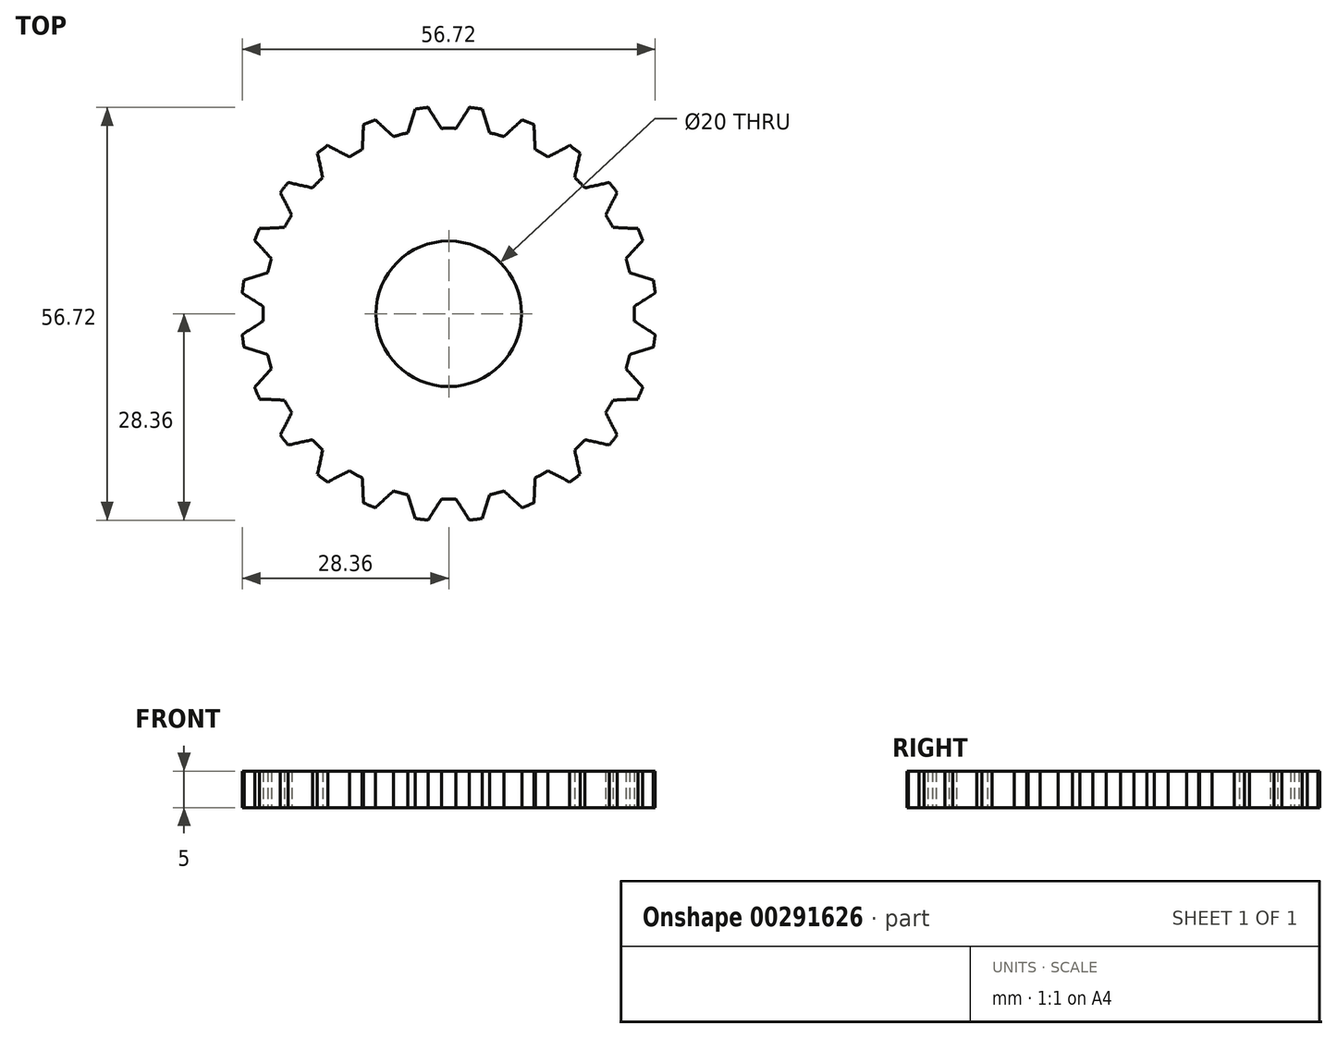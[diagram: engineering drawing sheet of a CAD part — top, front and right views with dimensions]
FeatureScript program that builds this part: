
annotation { "Feature Type Name" : "Feature", "Feature Type Description" : "" }
export const myFeature = defineFeature(function(context is Context, id is Id, definition is map)
    precondition{}
    {
        {
            assignVariable(context, id + "F0", {"name" : "pin", "anyValue" : 24});
        }
        {
            assignVariable(context, id + "F1", {"name" : "Thickness", "anyValue" : 5});
        }
        {
            var Q0;
            Q0=qCreatedBy(makeId("Front.planeOp"),FACE);
            var sketch = newSketch(context, id + "F2", { "sketchPlane" : qUnion([Q0])});
            skLineSegment(sketch, "E0", {"start": v(0, 0) * mm, "end": v(0, 5) * mm, "construction": true});
            skSolve(sketch);
        }
        {
            var Q0;
            Q0=qCreatedBy(makeId("Top.planeOp"),FACE);
            var sketch = newSketch(context, id + "F3", { "sketchPlane" : qUnion([Q0])});
            skCircle(sketch, "E1", {"center": v(0, 0) * mm, "radius": 24 * mm, "construction": true});
            skLineSegment(sketch, "E2", {"start": v(0, 0) * mm, "end": v(24, 0) * mm, "construction": true});
            skLineSegment(sketch, "E3", {"start": v(0, 0) * mm, "end": v(23.18, 6.21) * mm, "construction": true});
            skLineSegment(sketch, "E4", {"start": v(23.18, 6.21) * mm, "end": v(24, 0) * mm, "construction": true});
            skLineSegment(sketch, "E5", {"start": v(0, 0) * mm, "end": v(23.6, 3.1) * mm, "construction": true});
            skLineSegment(sketch, "E6", {"start": v(23.18, 6.21) * mm, "end": v(29.74, 3.92) * mm, "construction": true});
            skLineSegment(sketch, "E7", {"start": v(29.74, 3.92) * mm, "end": v(24, 0) * mm, "construction": true});
            skFitSpline(sketch, "E8", {"points": [v(23.18, 6.21) * mm, v(29.74, 3.92) * mm, v(24, 0) * mm], "startDerivative": vector(29.8, -10.5) * mm, "endDerivative": vector(-26.07, -17.85) * mm});
            skCircle(sketch, "E9", {"center": v(0, 0) * mm, "radius": 10 * mm});
            skLineSegment(sketch, "E10", {"start": v(29.74, 3.92) * mm, "end": v(23.8, 3.13) * mm, "construction": true});
            skCircle(sketch, "E11", {"center": v(0, 0) * mm, "radius": 28.5 * mm});
            skCircle(sketch, "E12", {"center": v(0, 0) * mm, "radius": 25.5 * mm});
            skLineSegment(sketch, "E13", {"start": v(28.15, 4.46) * mm, "end": v(28.34, 2.98) * mm, "construction": true});
            skSolve(sketch);
        }
        {
            var Q0;
            Q0=makeQuery(id+"F3.imprint","IMPRINT",FACE,{"disambiguationData":[TD([[makeQuery(id+"F3.imprint","IMPRINT",EDGE,{"derivedFrom":sQuery(id+"F3.wireOp",EDGE,"E9")}),-1.0]])]});
            var Q1;
            {var subQ0=sQuery(id+"F3.wireOp",EDGE,"E11");var subQ1=sQuery(id+"F3.wireOp",EDGE,"E8");var subQ2=makeQuery(id+"F3.imprint","INTERSECT",VERTEX,{"disambiguationData":[OD(0.0)],"derivedFrom":[subQ1,subQ0]});Q1=makeQuery(id+"F3.imprint","IMPRINT",FACE,{"disambiguationData":[TD([[makeQuery(id+"F3.imprint","IMPRINT",EDGE,{"disambiguationData":[TD([[subQ2,1.0]])],"derivedFrom":subQ1}),-1.0]])]});}
            extrude(context, id + "F4", {"entities" : qUnion([Q0, Q1]), "depth" : (getVariable(context, 'Thickness')) * mm});
        }
        {
            var Q0;
            Q0=makeQuery(id+"F4.opExtrude","SWEPT_BODY",BODY,{"disambiguationData":[OSD([sQuery(id+"F3.wireOp",EDGE,"E8"),sQuery(id+"F3.wireOp",EDGE,"E9"),sQuery(id+"F3.wireOp",EDGE,"E11"),sQuery(id+"F3.wireOp",EDGE,"E12")])]});
            var Q1;
            Q1=sQuery(id+"F2.wireOp",EDGE,"E0");
            circularPattern(context, id + "F5", {"operationType" : NewBodyOperationType.ADD, "entities" : qUnion([Q0]), "axis" : qUnion([Q1]), "angle" : 360 * degree, "instanceCount" : getVariable(context, 'pin'), "equalSpace" : true});
        }
    });
